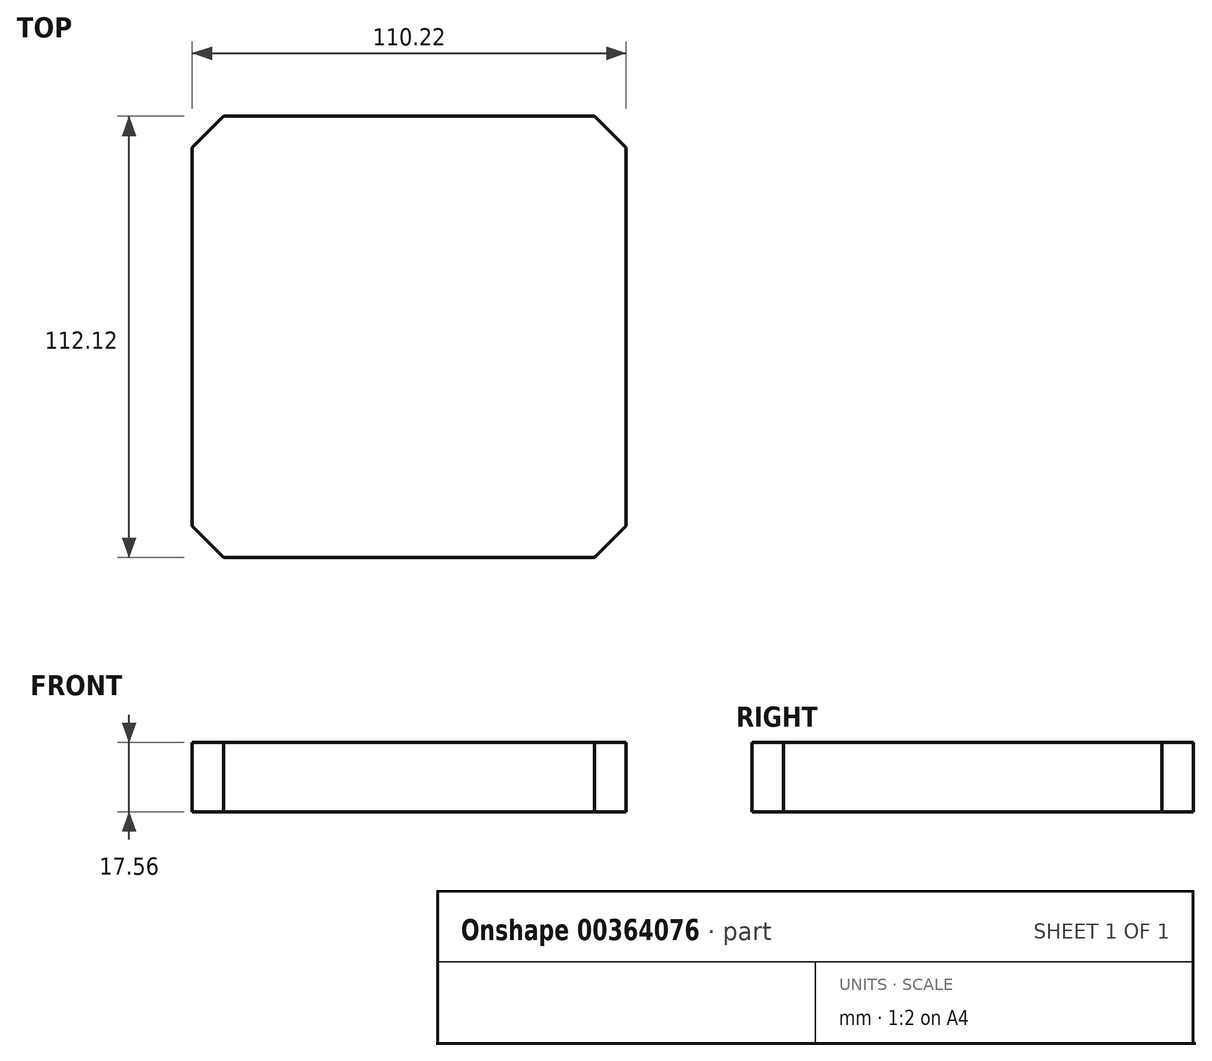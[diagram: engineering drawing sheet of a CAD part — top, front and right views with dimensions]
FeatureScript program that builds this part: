
annotation { "Feature Type Name" : "Feature", "Feature Type Description" : "" }
export const myFeature = defineFeature(function(context is Context, id is Id, definition is map)
    precondition{}
    {
        {
            var Q0;
            Q0=qCreatedBy(makeId("Top.planeOp"),FACE);
            var sketch = newSketch(context, id + "F0", { "sketchPlane" : qUnion([Q0])});
            skLineSegment(sketch, "E0.bottom", {"start": v(0, 0) * mm, "end": v(0, 0) * mm});
            skLineSegment(sketch, "E0.top", {"start": v(0, 0) * mm, "end": v(0, 0) * mm});
            skLineSegment(sketch, "E0.left", {"start": v(0, 0) * mm, "end": v(0, 0) * mm});
            skLineSegment(sketch, "E0.right", {"start": v(0, 0) * mm, "end": v(0, 0) * mm});
            skPoint(sketch, "E0.middle", {"position": v(0, 0) * mm});
            skLineSegment(sketch, "E1.bottom", {"start": v(55.11, 56.06) * mm, "end": v(-55.11, 56.06) * mm});
            skLineSegment(sketch, "E1.top", {"start": v(55.11, -56.06) * mm, "end": v(-55.11, -56.06) * mm});
            skLineSegment(sketch, "E1.left", {"start": v(55.11, 56.06) * mm, "end": v(55.11, -56.06) * mm});
            skLineSegment(sketch, "E1.right", {"start": v(-55.11, 56.06) * mm, "end": v(-55.11, -56.06) * mm});
            skSolve(sketch);
        }
        {
            var Q0;
            Q0=makeQuery(id+"F0.imprint","IMPRINT",FACE,{"disambiguationData":[TD([[makeQuery(id+"F0.imprint","IMPRINT",EDGE,{"derivedFrom":sQuery(id+"F0.wireOp",EDGE,"E1.bottom")}),1.0]])]});
            extrude(context, id + "F1", {"entities" : qUnion([Q0]), "depth" : 17.56 * mm});
        }
        {
            var Q0;
            Q0=makeQuery(id+"F1.opExtrude","SWEPT_EDGE",EDGE,{"disambiguationData":[OSD([sQuery(id+"F0.wireOp",EDGE,"E1.bottom"),sQuery(id+"F0.wireOp",EDGE,"E1.right")])]});
            var Q1;
            Q1=makeQuery(id+"F1.opExtrude","SWEPT_EDGE",EDGE,{"disambiguationData":[OSD([sQuery(id+"F0.wireOp",EDGE,"E1.top"),sQuery(id+"F0.wireOp",EDGE,"E1.right")])]});
            var Q2;
            Q2=makeQuery(id+"F1.opExtrude","SWEPT_EDGE",EDGE,{"disambiguationData":[OSD([sQuery(id+"F0.wireOp",EDGE,"E1.bottom"),sQuery(id+"F0.wireOp",EDGE,"E1.left")])]});
            var Q3;
            Q3=makeQuery(id+"F1.opExtrude","SWEPT_EDGE",EDGE,{"disambiguationData":[OSD([sQuery(id+"F0.wireOp",EDGE,"E1.top"),sQuery(id+"F0.wireOp",EDGE,"E1.left")])]});
            chamfer(context, id + "F2", {"entities" : qUnion([Q0, Q1, Q2, Q3]), "width" : 8 * mm, "tangentPropagation" : true});
        }
    });
